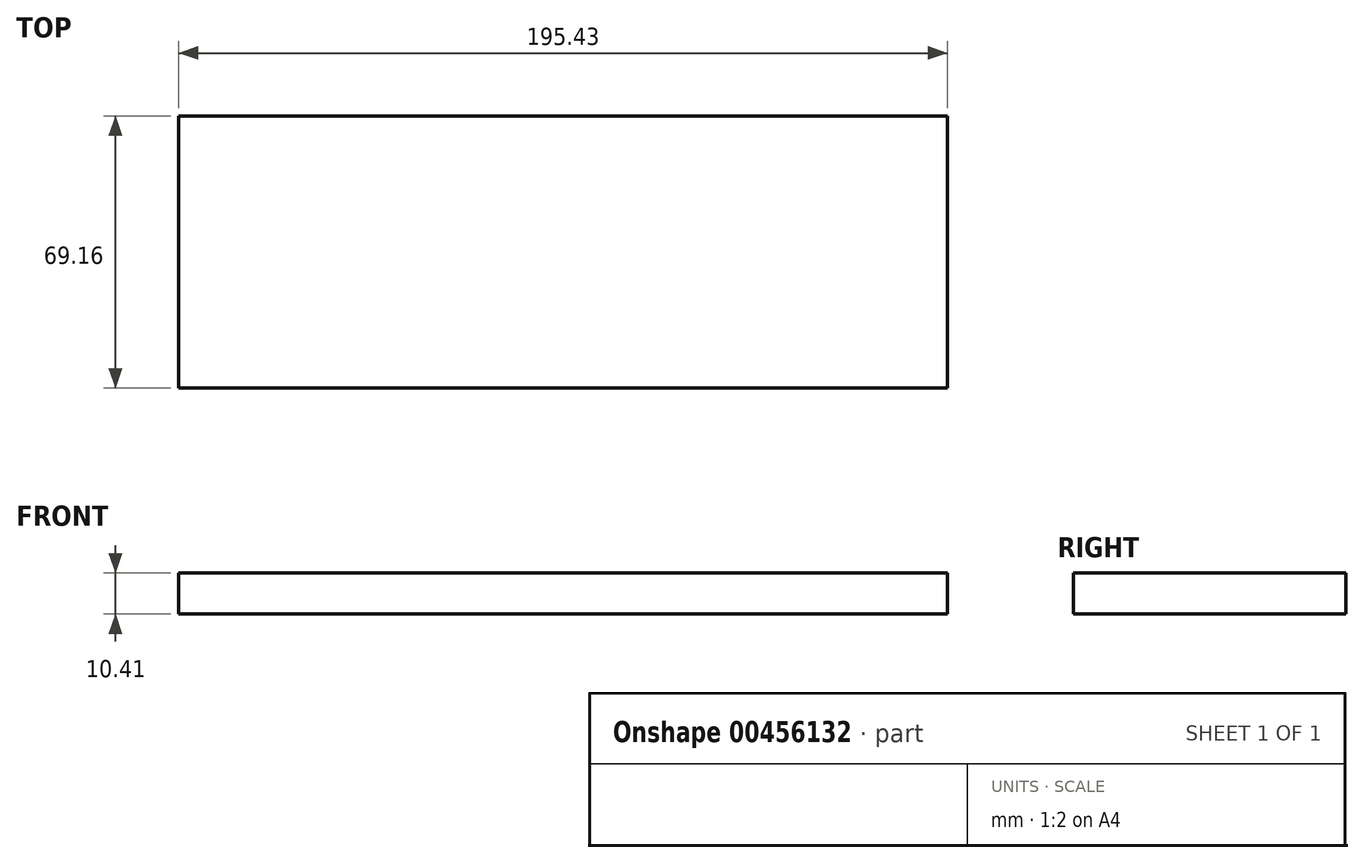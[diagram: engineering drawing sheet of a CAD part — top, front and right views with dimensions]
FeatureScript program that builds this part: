
annotation { "Feature Type Name" : "Feature", "Feature Type Description" : "" }
export const myFeature = defineFeature(function(context is Context, id is Id, definition is map)
    precondition{}
    {
        {
            var Q0;
            Q0=qCreatedBy(makeId("Top.planeOp"),FACE);
            var sketch = newSketch(context, id + "F0", { "sketchPlane" : qUnion([Q0])});
            skLineSegment(sketch, "E0.bottom", {"start": v(-96.76, 51.8) * mm, "end": v(98.67, 51.8) * mm});
            skLineSegment(sketch, "E0.top", {"start": v(-96.76, -17.37) * mm, "end": v(98.67, -17.37) * mm});
            skLineSegment(sketch, "E0.left", {"start": v(-96.76, 51.8) * mm, "end": v(-96.76, -17.37) * mm});
            skLineSegment(sketch, "E0.right", {"start": v(98.67, 51.8) * mm, "end": v(98.67, -17.37) * mm});
            skSolve(sketch);
        }
        {
            var Q0;
            Q0=makeQuery(id+"F0.imprint","IMPRINT",FACE,{"disambiguationData":[TD([[makeQuery(id+"F0.imprint","IMPRINT",EDGE,{"derivedFrom":sQuery(id+"F0.wireOp",EDGE,"E0.bottom")}),-1.0]])]});
            extrude(context, id + "F1", {"entities" : qUnion([Q0]), "depth" : 10.4 * mm});
        }
    });
